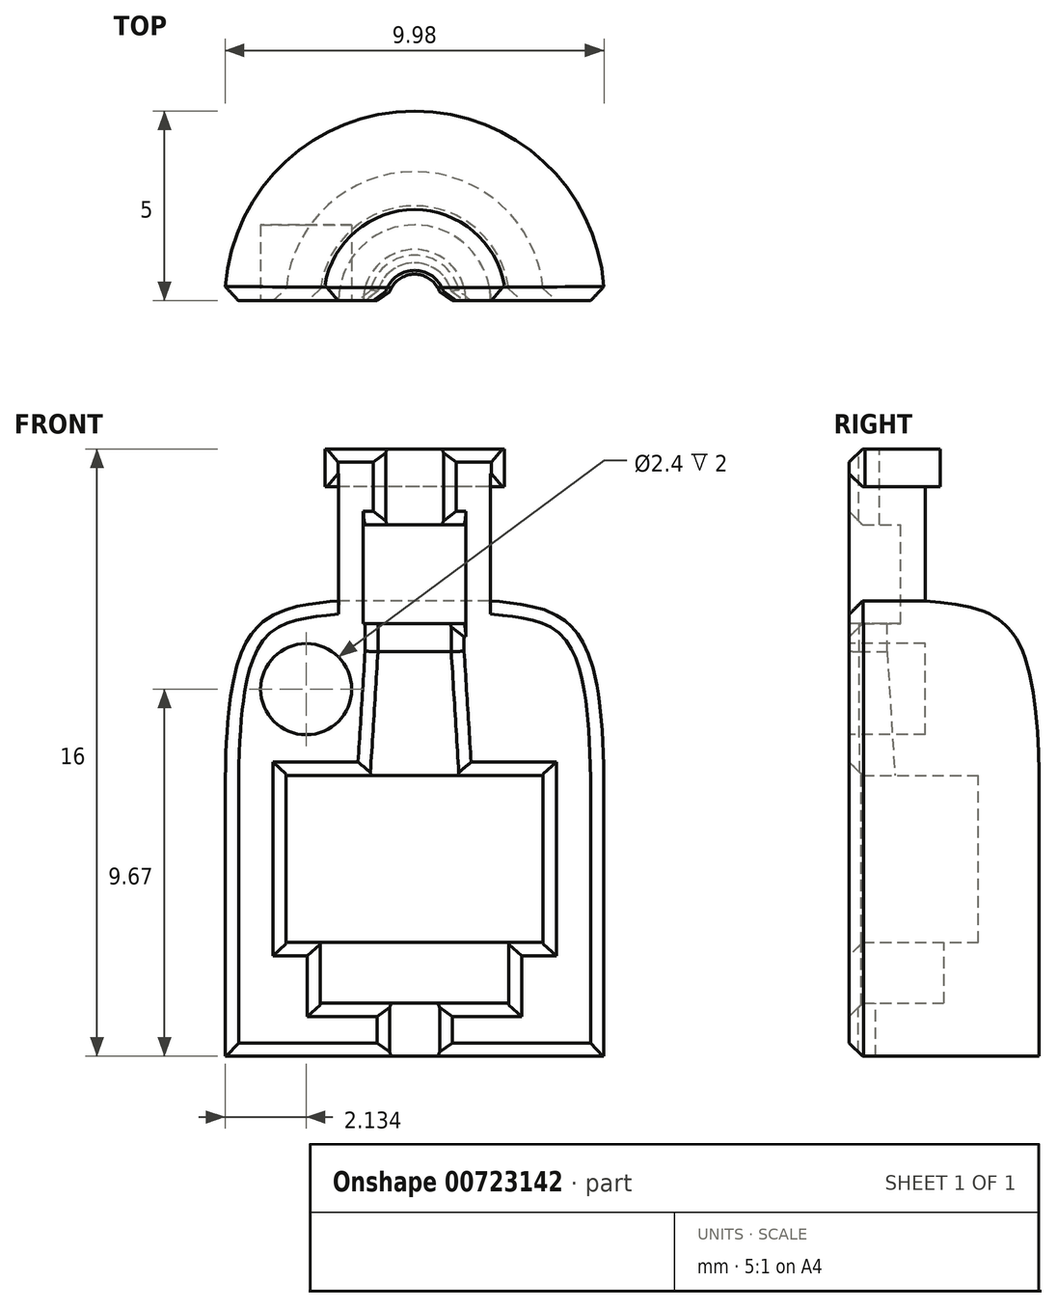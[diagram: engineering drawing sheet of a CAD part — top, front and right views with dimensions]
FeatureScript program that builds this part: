
annotation { "Feature Type Name" : "Feature", "Feature Type Description" : "" }
export const myFeature = defineFeature(function(context is Context, id is Id, definition is map)
    precondition{}
    {
        {
            var Q0;
            Q0=qCreatedBy(makeId("Front.planeOp"),FACE);
            var sketch = newSketch(context, id + "F0", { "sketchPlane" : qUnion([Q0])});
            skLineSegment(sketch, "E0", {"start": v(-0.7, 0) * mm, "end": v(-0.7, 1.4) * mm});
            skLineSegment(sketch, "E1", {"start": v(-0.7, 1.4) * mm, "end": v(-2.5, 1.4) * mm});
            skLineSegment(sketch, "E2", {"start": v(-2.5, 1.4) * mm, "end": v(-2.5, 3) * mm});
            skLineSegment(sketch, "E3", {"start": v(-2.5, 3) * mm, "end": v(-3.4, 3) * mm});
            skLineSegment(sketch, "E4", {"start": v(-3.4, 3) * mm, "end": v(-3.4, 7.4) * mm});
            skLineSegment(sketch, "E5", {"start": v(-3.4, 7.4) * mm, "end": v(-1, 7.4) * mm});
            skLineSegment(sketch, "E6", {"start": v(-1, 7.4) * mm, "end": v(-1, 11.4) * mm});
            skLineSegment(sketch, "E7", {"start": v(-1, 11.4) * mm, "end": v(-1.35, 11.4) * mm});
            skLineSegment(sketch, "E8", {"start": v(-1.35, 11.4) * mm, "end": v(-1.35, 14) * mm});
            skLineSegment(sketch, "E9", {"start": v(-1.35, 14) * mm, "end": v(-0.8, 14) * mm});
            skLineSegment(sketch, "E10", {"start": v(-0.8, 14) * mm, "end": v(-0.8, 16) * mm});
            skLineSegment(sketch, "E11", {"start": v(-0.8, 16) * mm, "end": v(-2.4, 16) * mm});
            skLineSegment(sketch, "E12", {"start": v(-2.4, 16) * mm, "end": v(-2.4, 15) * mm});
            skLineSegment(sketch, "E13", {"start": v(-2.4, 15) * mm, "end": v(-2, 15) * mm});
            skLineSegment(sketch, "E14", {"start": v(-2, 15) * mm, "end": v(-2, 12) * mm});
            skLineSegment(sketch, "E15", {"start": v(-5, 0) * mm, "end": v(-5, 6.96) * mm});
            skFitSpline(sketch, "E16", {"points": [v(-2, 12) * mm, v(-5, 6.96) * mm], "startDerivative": vector(-6.45, -0.6) * mm, "endDerivative": vector(0, -13.85) * mm});
            skCircle(sketch, "E17", {"center": v(-2.86, 9.67) * mm, "radius": 1.2 * mm});
            skLineSegment(sketch, "E18", {"start": v(-5, 0) * mm, "end": v(-0.7, 0) * mm});
            skLineSegment(sketch, "E19", {"start": v(0, 0) * mm, "end": v(0, 25.38) * mm, "construction": true});
            skCircle(sketch, "E20.MirrorC", {"center": v(2.86, 9.67) * mm, "radius": 1.2 * mm});
            skPoint(sketch, "E21", {"position": v(-4.17, 11.3) * mm});
            skLineSegment(sketch, "E22", {"start": v(-1, 10.66) * mm, "end": v(-1.2, 7.4) * mm});
            skSolve(sketch);
        }
        {
            var Q0;
            Q0=makeQuery(id+"F0.imprint","IMPRINT",FACE,{"disambiguationData":[TD([[makeQuery(id+"F0.imprint","IMPRINT",EDGE,{"derivedFrom":sQuery(id+"F0.wireOp",EDGE,"E0")}),1.0]])]});
            var Q1;
            Q1=makeQuery(id+"F0.imprint","IMPRINT",FACE,{"disambiguationData":[TD([[makeQuery(id+"F0.imprint","IMPRINT",EDGE,{"derivedFrom":sQuery(id+"F0.wireOp",EDGE,"E17")}),1.0]])]});
            var Q2;
            Q2=sQuery(id+"F0.wireOp",EDGE,"E19");
            revolve(context, id + "F1", {"surfaceOperationType" : NewSurfaceOperationType.NEW, "entities" : qUnion([Q0, Q1]), "axis" : qUnion([Q2]), "revolveType" : RevolveType.ONE_DIRECTION, "oppositeDirection" : true, "angle" : 180 * degree});
        }
        {
            var Q0;
            Q0=makeQuery(id+"F0.imprint","IMPRINT",FACE,{"disambiguationData":[TD([[makeQuery(id+"F0.imprint","IMPRINT",EDGE,{"derivedFrom":sQuery(id+"F0.wireOp",EDGE,"E20.MirrorC")}),-1.0]])]});
            var Q1;
            Q1=makeQuery(id+"F0.imprint","IMPRINT",FACE,{"disambiguationData":[TD([[makeQuery(id+"F0.imprint","IMPRINT",EDGE,{"derivedFrom":sQuery(id+"F0.wireOp",EDGE,"E17")}),1.0]])]});
            extrude(context, id + "F2", {"entities" : qUnion([Q0, Q1]), "operationType" : NewBodyOperationType.REMOVE, "oppositeDirection" : true, "depth" : 2 * mm, "offsetDistance" : 25 * mm});
        }
        {
            var Q0;
            Q0=makeQuery(id+"F1.opRevolve","CAP_EDGE",EDGE,{"disambiguationData":[OSD([sQuery(id+"F0.wireOp",EDGE,"E5")])],"isStart":false});
            var Q1;
            Q1=makeQuery(id+"F1.opRevolve","CAP_EDGE",EDGE,{"disambiguationData":[OSD([sQuery(id+"F0.wireOp",EDGE,"E4")])],"isStart":false});
            var Q2;
            Q2=makeQuery(id+"F1.opRevolve","CAP_EDGE",EDGE,{"disambiguationData":[OSD([sQuery(id+"F0.wireOp",EDGE,"E16")])],"isStart":false});
            var Q3;
            Q3=makeQuery(id+"F1.opRevolve","CAP_EDGE",EDGE,{"disambiguationData":[OSD([sQuery(id+"F0.wireOp",EDGE,"E15")])],"isStart":false});
            var Q4;
            Q4=makeQuery(id+"F1.opRevolve","CAP_EDGE",EDGE,{"disambiguationData":[OSD([sQuery(id+"F0.wireOp",EDGE,"E22")])],"isStart":false});
            var Q5;
            Q5=makeQuery(id+"F1.opRevolve","CAP_EDGE",EDGE,{"disambiguationData":[OSD([sQuery(id+"F0.wireOp",EDGE,"E3")])],"isStart":false});
            var Q6;
            Q6=makeQuery(id+"F1.opRevolve","CAP_EDGE",EDGE,{"disambiguationData":[OSD([sQuery(id+"F0.wireOp",EDGE,"E2")])],"isStart":false});
            var Q7;
            Q7=makeQuery(id+"F1.opRevolve","CAP_EDGE",EDGE,{"disambiguationData":[OSD([sQuery(id+"F0.wireOp",EDGE,"E0")])],"isStart":false});
            var Q8;
            Q8=makeQuery(id+"F1.opRevolve","CAP_EDGE",EDGE,{"disambiguationData":[OSD([sQuery(id+"F0.wireOp",EDGE,"E1")])],"isStart":false});
            var Q9;
            Q9=makeQuery(id+"F1.opRevolve","CAP_EDGE",EDGE,{"disambiguationData":[OSD([sQuery(id+"F0.wireOp",EDGE,"E18")])],"isStart":false});
            var Q10;
            Q10=makeQuery(id+"F1.opRevolve","CAP_EDGE",EDGE,{"disambiguationData":[OSD([sQuery(id+"F0.wireOp",EDGE,"E6")])],"isStart":false});
            var Q11;
            Q11=makeQuery(id+"F1.opRevolve","CAP_EDGE",EDGE,{"disambiguationData":[OSD([sQuery(id+"F0.wireOp",EDGE,"E7")])],"isStart":false});
            var Q12;
            Q12=makeQuery(id+"F1.opRevolve","CAP_EDGE",EDGE,{"disambiguationData":[OSD([sQuery(id+"F0.wireOp",EDGE,"E9")])],"isStart":false});
            var Q13;
            Q13=makeQuery(id+"F1.opRevolve","CAP_EDGE",EDGE,{"disambiguationData":[OSD([sQuery(id+"F0.wireOp",EDGE,"E10")])],"isStart":false});
            var Q14;
            Q14=makeQuery(id+"F1.opRevolve","CAP_EDGE",EDGE,{"disambiguationData":[OSD([sQuery(id+"F0.wireOp",EDGE,"E12")])],"isStart":false});
            var Q15;
            Q15=makeQuery(id+"F1.opRevolve","CAP_EDGE",EDGE,{"disambiguationData":[OSD([sQuery(id+"F0.wireOp",EDGE,"E13")])],"isStart":false});
            var Q16;
            Q16=makeQuery(id+"F1.opRevolve","CAP_EDGE",EDGE,{"disambiguationData":[OSD([sQuery(id+"F0.wireOp",EDGE,"E11")])],"isStart":false});
            var Q17;
            Q17=makeQuery(id+"F2.boolean.opBoolean","COPY",EDGE,{"derivedFrom":makeQuery(id+"F2.opExtrude","CAP_EDGE",EDGE,{"disambiguationData":[OSD([sQuery(id+"F0.wireOp",EDGE,"E20.MirrorC")])],"isStart":true})});
            var Q18;
            Q18=makeQuery(id+"F1.opRevolve","CAP_EDGE",EDGE,{"disambiguationData":[OSD([sQuery(id+"F0.wireOp",EDGE,"E9")])],"isStart":true});
            var Q19;
            Q19=makeQuery(id+"F1.opRevolve","CAP_EDGE",EDGE,{"disambiguationData":[OSD([sQuery(id+"F0.wireOp",EDGE,"E10")])],"isStart":true});
            var Q20;
            Q20=makeQuery(id+"F1.opRevolve","CAP_EDGE",EDGE,{"disambiguationData":[OSD([sQuery(id+"F0.wireOp",EDGE,"E11")])],"isStart":true});
            var Q21;
            Q21=makeQuery(id+"F1.opRevolve","CAP_EDGE",EDGE,{"disambiguationData":[OSD([sQuery(id+"F0.wireOp",EDGE,"E12")])],"isStart":true});
            var Q22;
            Q22=makeQuery(id+"F1.opRevolve","CAP_EDGE",EDGE,{"disambiguationData":[OSD([sQuery(id+"F0.wireOp",EDGE,"E13")])],"isStart":true});
            var Q23;
            Q23=makeQuery(id+"F1.opRevolve","CAP_EDGE",EDGE,{"disambiguationData":[OSD([sQuery(id+"F0.wireOp",EDGE,"E16")])],"isStart":true});
            var Q24;
            Q24=makeQuery(id+"F2.boolean.opBoolean","COPY",EDGE,{"derivedFrom":makeQuery(id+"F2.opExtrude","CAP_EDGE",EDGE,{"disambiguationData":[OSD([sQuery(id+"F0.wireOp",EDGE,"E17")])],"isStart":true})});
            var Q25;
            Q25=makeQuery(id+"F1.opRevolve","CAP_EDGE",EDGE,{"disambiguationData":[OSD([sQuery(id+"F0.wireOp",EDGE,"E22")])],"isStart":true});
            var Q26;
            Q26=makeQuery(id+"F1.opRevolve","CAP_EDGE",EDGE,{"disambiguationData":[OSD([sQuery(id+"F0.wireOp",EDGE,"E6")])],"isStart":true});
            var Q27;
            Q27=makeQuery(id+"F1.opRevolve","CAP_EDGE",EDGE,{"disambiguationData":[OSD([sQuery(id+"F0.wireOp",EDGE,"E5")])],"isStart":true});
            var Q28;
            Q28=makeQuery(id+"F1.opRevolve","CAP_EDGE",EDGE,{"disambiguationData":[OSD([sQuery(id+"F0.wireOp",EDGE,"E4")])],"isStart":true});
            var Q29;
            Q29=makeQuery(id+"F1.opRevolve","CAP_EDGE",EDGE,{"disambiguationData":[OSD([sQuery(id+"F0.wireOp",EDGE,"E3")])],"isStart":true});
            var Q30;
            Q30=makeQuery(id+"F1.opRevolve","CAP_EDGE",EDGE,{"disambiguationData":[OSD([sQuery(id+"F0.wireOp",EDGE,"E2")])],"isStart":true});
            var Q31;
            Q31=makeQuery(id+"F1.opRevolve","CAP_EDGE",EDGE,{"disambiguationData":[OSD([sQuery(id+"F0.wireOp",EDGE,"E1")])],"isStart":true});
            var Q32;
            Q32=makeQuery(id+"F1.opRevolve","CAP_EDGE",EDGE,{"disambiguationData":[OSD([sQuery(id+"F0.wireOp",EDGE,"E0")])],"isStart":true});
            var Q33;
            Q33=makeQuery(id+"F1.opRevolve","CAP_EDGE",EDGE,{"disambiguationData":[OSD([sQuery(id+"F0.wireOp",EDGE,"E18")])],"isStart":true});
            chamfer(context, id + "F3", {"entities" : qUnion([Q0, Q1, Q2, Q3, Q4, Q5, Q6, Q7, Q8, Q9, Q10, Q11, Q12, Q13, Q14, Q15, Q16, Q17, Q18, Q19, Q20, Q21, Q22, Q23, Q24, Q25, Q26, Q27, Q28, Q29, Q30, Q31, Q32, Q33]), "width" : 0.35 * mm, "tangentPropagation" : true});
        }
    });
